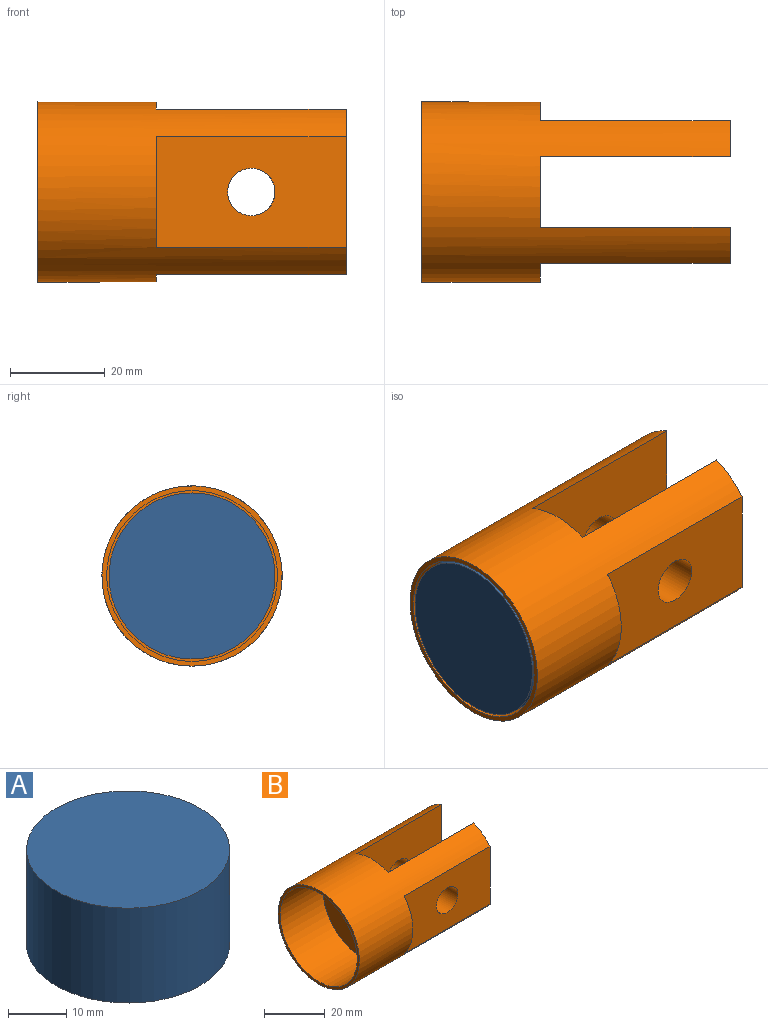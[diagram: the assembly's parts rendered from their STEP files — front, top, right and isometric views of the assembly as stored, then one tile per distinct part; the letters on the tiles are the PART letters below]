
ASSEMBLY  parts=2 mates=1
PART A: 3 faces, bbox 35x35x20 mm
  f0: cylinder r=17.5mm len=35mm, axis (0,0,-1), area 2199.1mm2, adj f1,f2
  f1: plane 35x35mm, normal (0,0,1), area 962.1mm2, adj f0
  f2: plane 35x35mm, normal (0,0,-1), area 962.1mm2, adj f0
PART B: 17 faces, bbox 65x38x38 mm
  f0: plane 38x15mm, normal (1,0,0), area 476.3mm2, adj f2,f6,f9,f13
  f1: plane 23.32x4mm, normal (1,0,0), area 63.6mm2, adj f2,f8
  f2: cylinder r=19mm len=65mm, axis (-1,0,0), area 4517.2mm2, adj f0,f1,f3,f4,f5,f6,f7,f8
  f3: plane 23.32x4mm, normal (1,0,0), area 63.6mm2, adj f2,f5
  f4: plane 38x38mm, normal (-1,0,0), area 116.2mm2, adj f2,f15
  f5: plane 40x23.32mm, normal (0,-1,0), area 854.4mm2, adj f2,f3,f7,f12
  f6: plane 40x34.91mm, normal (0,1,0), area 1318mm2, adj f0,f2,f7,f12
  f7: plane 34.91x7.5mm, normal (1,0,0), area 226mm2, adj f2,f5,f6
  f8: plane 40x23.32mm, normal (0,1,0), area 854.4mm2, adj f1,f2,f10,f11
  f9: plane 40x34.91mm, normal (0,-1,0), area 1318mm2, adj f0,f2,f10,f11
  f10: plane 34.91x7.5mm, normal (1,0,0), area 226mm2, adj f2,f8,f9
  f11: cylinder r=5mm len=10mm, axis (0,-1,0), area 235.6mm2, adj f8,f9
  f12: cylinder r=5mm len=10mm, axis (0,-1,0), area 235.6mm2, adj f5,f6
  f13: cylinder r=5mm len=10mm, axis (1,0,0), area 125.7mm2, adj f0,f14
  f14: plane 10x10mm, normal (1,0,0), area 78.5mm2, adj f13
  f15: cylinder r=18mm len=36mm, axis (-1,0,0), area 2261.9mm2, adj f4,f16
  f16: plane 36x36mm, normal (-1,0,0), area 1017.9mm2, adj f15
PLACE A rot(axis=(0.71,0,0.71),180deg) t=(-38.91,-10.85,45.59)mm
PLACE B t=(-38.91,-10.85,45.59)mm
MATE parallel A.f0 <-> B.f15  axis (1,0,0) through (-18.91,-10.85,45.59)mm
